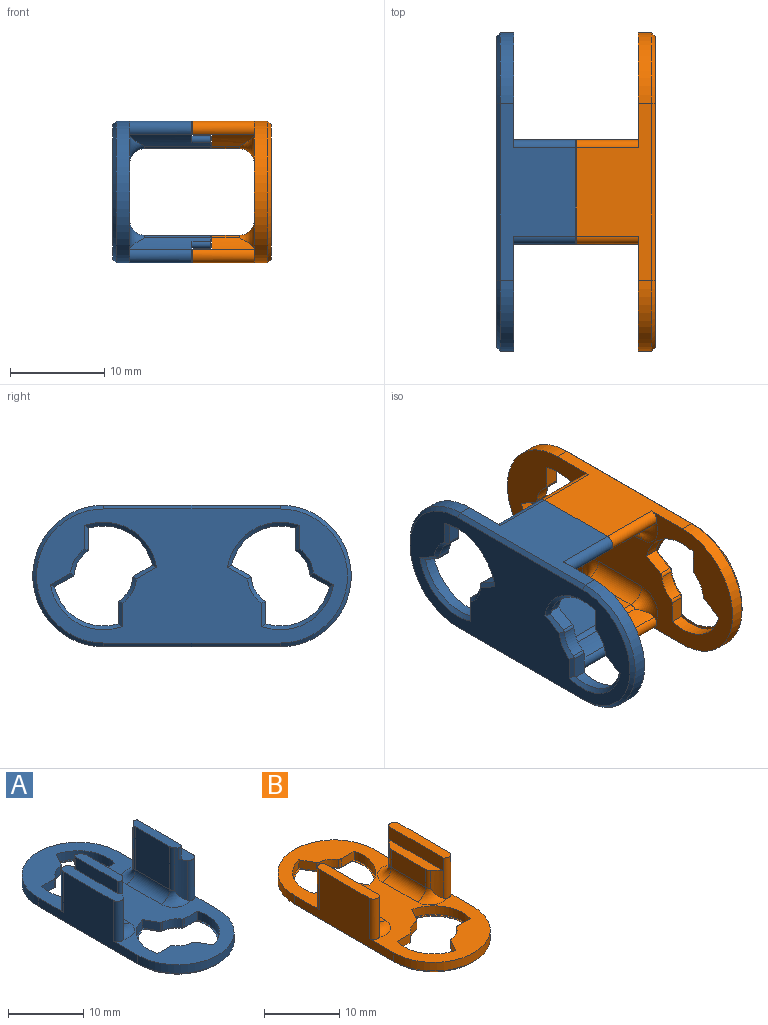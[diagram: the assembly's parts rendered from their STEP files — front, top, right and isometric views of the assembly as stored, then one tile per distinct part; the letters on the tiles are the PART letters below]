
ASSEMBLY  parts=2 mates=1
PART A: 84 faces, bbox 15x33.8x10.4 mm
  f0: plane 11x2.24mm, normal (0,0,1), area 17mm2, adj f3,f15,f16,f20,f21,f60,f64,f65
  f1: plane 32.95x14.2mm, normal (0,0,-1), area 269mm2, adj f22,f23,f24,f25,f48,f49,f50,f51
  f2: plane 33.75x15mm, normal (0,0,1), area 226mm2, adj f3,f5,f7,f8,f9,f14,f15,f21
  f3: plane 18.75x8mm, normal (1,0,0), area 88.3mm2, adj f0,f2,f7,f8,f15,f21,f23
  f4: plane 7x6.49mm, normal (1,0,0), area 45.4mm2, adj f11,f12,f30,f63
  f5: plane 18.75x8mm, normal (-1,0,0), area 88.3mm2, adj f2,f6,f7,f8,f9,f14,f24
  f6: plane 11x2.24mm, normal (0,0,1), area 17mm2, adj f5,f9,f10,f13,f14,f62,f66,f67
  f7: cylinder r=7.5mm len=15mm, axis (0,0,-1), area 33mm2, adj f2,f3,f5,f22
  f8: cylinder r=7.5mm len=15mm, axis (0,0,-1), area 33mm2, adj f2,f3,f5,f25
  f9: cylinder r=0.8mm len=6.6mm, axis (0,0,1), area 13.4mm2, adj f2,f5,f6,f10,f29
  f10: cylinder r=7.37mm len=8.55mm, axis (0,0,1), area 11.6mm2, adj f6,f9,f11,f29,f63,f66
  f11: cylinder r=0.8mm len=7mm, axis (0,0,1), area 4.8mm2, adj f4,f10,f29,f63
  f12: cylinder r=0.8mm len=7mm, axis (0,0,1), area 4.8mm2, adj f4,f13,f31,f63
  f13: cylinder r=7.37mm len=8.55mm, axis (0,0,1), area 11.6mm2, adj f6,f12,f14,f31,f63,f67
  f14: cylinder r=0.8mm len=6.6mm, axis (0,0,1), area 13.4mm2, adj f2,f5,f6,f13,f31
  f15: cylinder r=0.8mm len=6.6mm, axis (0,0,1), area 13.4mm2, adj f0,f2,f3,f16,f26
  f16: cylinder r=7.37mm len=8.55mm, axis (0,0,1), area 11.6mm2, adj f0,f15,f17,f26,f61,f64
  f17: cylinder r=0.8mm len=7mm, axis (0,0,1), area 4.8mm2, adj f16,f18,f26,f61
  f18: plane 7x6.49mm, normal (-1,0,0), area 45.4mm2, adj f17,f19,f27,f61
  f19: cylinder r=0.8mm len=7mm, axis (0,0,1), area 4.8mm2, adj f18,f20,f28,f61
  f20: cylinder r=7.37mm len=8.55mm, axis (0,0,1), area 11.6mm2, adj f0,f19,f21,f28,f61,f65
  f21: cylinder r=0.8mm len=6.6mm, axis (0,0,1), area 13.4mm2, adj f0,f2,f3,f20,f28
  f22: cone r=7.5mm half-angle=45deg, axis (0,0,1), area 13mm2, adj f1,f7,f23,f24
  f23: plane 18.75x0.4mm, normal (0.71,0,-0.71), area 10.6mm2, adj f1,f3,f22,f25
  f24: plane 18.75x0.4mm, normal (-0.71,0,-0.71), area 10.6mm2, adj f1,f5,f22,f25
  f25: cone r=7.5mm half-angle=45deg, axis (0,0,1), area 13mm2, adj f1,f8,f23,f24
  f26: torus R=2.4mm, axis (0,0,1), area 5.8mm2, adj f2,f15,f16,f17,f27
  f27: cylinder r=1.6mm len=6.49mm, axis (0,1,0), area 16.3mm2, adj f2,f18,f26,f28
  f28: torus R=2.4mm, axis (0,0,1), area 5.8mm2, adj f2,f19,f20,f21,f27
  f29: torus R=2.4mm, axis (0,0,1), area 5.8mm2, adj f2,f9,f10,f11,f30
  f30: cylinder r=1.6mm len=6.49mm, axis (0,-1,0), area 16.3mm2, adj f2,f4,f29,f31
  f31: torus R=2.4mm, axis (0,0,1), area 5.8mm2, adj f2,f12,f13,f14,f30
  f32: cylinder r=5.55mm len=6.98mm, axis (0,0,1), area 12.6mm2, adj f2,f33,f39,f68
  f33: plane 2.43x1.4mm, normal (0,-1,0), area 3.4mm2, adj f2,f32,f55,f68,f78
  f34: cylinder r=3.1mm len=2.3mm, axis (0,0,1), area 3.8mm2, adj f2,f57,f78,f79
  f35: plane 2.12x1.4mm, normal (-0.87,-0.5,0), area 3.4mm2, adj f2,f36,f59,f69,f79
  f36: cylinder r=5.55mm len=6.98mm, axis (0,0,1), area 12.6mm2, adj f2,f35,f37,f69
  f37: plane 2.43x1.4mm, normal (0,1,0), area 3.4mm2, adj f2,f36,f58,f69,f76
  f38: cylinder r=3.1mm len=2.3mm, axis (0,0,1), area 3.8mm2, adj f2,f56,f76,f77
  f39: plane 2.12x1.4mm, normal (0.87,0.5,0), area 3.4mm2, adj f2,f32,f54,f68,f77
  f40: plane 2.12x1.4mm, normal (-0.87,0.5,0), area 3.4mm2, adj f2,f47,f51,f71,f80
  f41: cylinder r=3.1mm len=2.3mm, axis (0,0,1), area 3.8mm2, adj f2,f52,f80,f83
  f42: plane 2.43x1.4mm, normal (0,1,0), area 3.4mm2, adj f2,f43,f53,f70,f83
  f43: cylinder r=5.55mm len=6.98mm, axis (0,0,1), area 12.6mm2, adj f2,f42,f44,f70
  f44: plane 2.12x1.4mm, normal (0.87,-0.5,0), area 3.4mm2, adj f2,f43,f50,f70,f82
  f45: cylinder r=3.1mm len=2.3mm, axis (0,0,1), area 3.8mm2, adj f2,f49,f81,f82
  f46: plane 2.43x1.4mm, normal (0,-1,0), area 3.4mm2, adj f2,f47,f48,f71,f81
  f47: cylinder r=5.55mm len=6.98mm, axis (0,0,1), area 12.6mm2, adj f2,f40,f46,f71
  f48: plane 2.67x0.42mm, normal (0,-0.71,-0.71), area 1.4mm2, adj f1,f46,f49,f74,f81
  f49: cone r=3.5mm half-angle=45deg, axis (0,0,-1), area 1.8mm2, adj f1,f45,f48,f50,f81,f82
  f50: plane 2.5x1.46mm, normal (0.61,-0.35,-0.71), area 1.4mm2, adj f1,f44,f49,f75,f82
  f51: plane 2.5x1.46mm, normal (-0.61,0.35,-0.71), area 1.4mm2, adj f1,f40,f52,f74,f80
  f52: cone r=3.5mm half-angle=45deg, axis (0,0,-1), area 1.8mm2, adj f1,f41,f51,f53,f80,f83
  f53: plane 2.67x0.42mm, normal (0,0.71,-0.71), area 1.4mm2, adj f1,f42,f52,f75,f83
  f54: plane 2.5x1.46mm, normal (0.61,0.35,-0.71), area 1.4mm2, adj f1,f39,f56,f72,f77
  f55: plane 2.67x0.42mm, normal (0,-0.71,-0.71), area 1.4mm2, adj f1,f33,f57,f72,f78
  f56: cone r=3.1mm half-angle=45deg, axis (0,0,-1), area 1.8mm2, adj f1,f38,f54,f58,f76,f77
  f57: cone r=3.1mm half-angle=45deg, axis (0,0,-1), area 1.8mm2, adj f1,f34,f55,f59,f78,f79
  f58: plane 2.67x0.42mm, normal (0,0.71,-0.71), area 1.4mm2, adj f1,f37,f56,f73,f76
  f59: plane 2.5x1.46mm, normal (-0.61,-0.35,-0.71), area 1.4mm2, adj f1,f35,f57,f73,f79
  f60: plane 7.88x2mm, normal (1,0,0), area 15.7mm2, adj f0,f61,f64,f65
  f61: plane 8.68x1.35mm, normal (0,0,1), area 11mm2, adj f16,f17,f18,f19,f20,f60,f64,f65
  f62: plane 7.88x2mm, normal (-1,0,0), area 15.7mm2, adj f6,f63,f66,f67
  f63: plane 8.68x1.35mm, normal (0,0,1), area 11mm2, adj f4,f10,f11,f12,f13,f62,f66,f67
  f64: cylinder r=0.4mm len=2mm, axis (0,0,1), area 1.9mm2, adj f0,f16,f60,f61
  f65: cylinder r=0.4mm len=2mm, axis (0,0,1), area 1.9mm2, adj f0,f20,f60,f61
  f66: cylinder r=0.4mm len=2mm, axis (0,0,1), area 1.9mm2, adj f6,f10,f62,f63
  f67: cylinder r=0.4mm len=2mm, axis (0,0,1), area 1.9mm2, adj f6,f13,f62,f63
  f68: plane 6.98x4.41mm, normal (0,0,1), area 2.2mm2, adj f32,f33,f39,f72
  f69: plane 6.98x4.41mm, normal (0,0,1), area 2.2mm2, adj f35,f36,f37,f73
  f70: plane 6.98x4.41mm, normal (0,0,1), area 2.2mm2, adj f42,f43,f44,f75
  f71: plane 6.98x4.41mm, normal (0,0,1), area 2.2mm2, adj f40,f46,f47,f74
  f72: cone r=5.7mm half-angle=45deg, axis (0,0,-1), area 5.3mm2, adj f1,f54,f55,f68
  f73: cone r=5.7mm half-angle=45deg, axis (0,0,-1), area 5.3mm2, adj f1,f58,f59,f69
  f74: cone r=5.7mm half-angle=45deg, axis (0,0,-1), area 5.3mm2, adj f1,f48,f51,f71
  f75: cone r=5.7mm half-angle=45deg, axis (0,0,-1), area 5.3mm2, adj f1,f50,f53,f70
  f76: cylinder r=0.4mm len=1.45mm, axis (0,0,1), area 0.6mm2, adj f2,f37,f38,f56,f58
  f77: cylinder r=0.4mm len=1.45mm, axis (0,0,1), area 0.5mm2, adj f2,f38,f39,f54,f56
  f78: cylinder r=0.4mm len=1.45mm, axis (0,0,1), area 0.6mm2, adj f2,f33,f34,f55,f57
  f79: cylinder r=0.4mm len=1.45mm, axis (0,0,1), area 0.5mm2, adj f2,f34,f35,f57,f59
  f80: cylinder r=0.4mm len=1.45mm, axis (0,0,1), area 0.5mm2, adj f2,f40,f41,f51,f52
  f81: cylinder r=0.4mm len=1.45mm, axis (0,0,1), area 0.6mm2, adj f2,f45,f46,f48,f49
  f82: cylinder r=0.4mm len=1.45mm, axis (0,0,1), area 0.5mm2, adj f2,f44,f45,f49,f50
  f83: cylinder r=0.4mm len=1.45mm, axis (0,0,1), area 0.6mm2, adj f2,f41,f42,f52,f53
PART B: 80 faces, bbox 15x33.8x8.4 mm
  f0: plane 2.5x1.46mm, normal (-0.61,0.35,-0.71), area 1.4mm2, adj f13,f53,f58,f70,f72
  f1: plane 2.67x0.42mm, normal (0,-0.71,-0.71), area 1.4mm2, adj f13,f51,f59,f70,f74
  f2: plane 2.67x0.42mm, normal (0,0.71,-0.71), area 1.4mm2, adj f13,f55,f58,f71,f73
  f3: plane 2.5x1.46mm, normal (0.61,-0.35,-0.71), area 1.4mm2, adj f13,f49,f59,f71,f75
  f4: plane 2.5x1.46mm, normal (0.61,0.35,-0.71), area 1.4mm2, adj f13,f41,f56,f69,f77
  f5: plane 2.67x0.42mm, normal (0,-0.71,-0.71), area 1.4mm2, adj f13,f43,f57,f69,f78
  f6: plane 2.67x0.42mm, normal (0,0.71,-0.71), area 1.4mm2, adj f13,f47,f56,f68,f76
  f7: plane 2.5x1.46mm, normal (-0.61,-0.35,-0.71), area 1.4mm2, adj f13,f45,f57,f68,f79
  f8: plane 6.49x2.9mm, normal (1,0,0), area 18.8mm2, adj f9,f23,f38,f63
  f9: cylinder r=0.8mm len=2.9mm, axis (0,0,1), area 2mm2, adj f8,f10,f39,f63
  f10: cylinder r=7.37mm len=4.45mm, axis (0,0,1), area 6.8mm2, adj f9,f24,f39,f63
  f11: cylinder r=0.8mm len=2.9mm, axis (0,0,1), area 2mm2, adj f12,f28,f36,f61
  f12: cylinder r=7.37mm len=4.45mm, axis (0,0,1), area 6.8mm2, adj f11,f29,f36,f61
  f13: plane 32.95x14.2mm, normal (0,0,-1), area 269mm2, adj f0,f1,f2,f3,f4,f5,f6,f7
  f14: plane 33.75x15mm, normal (0,0,1), area 226mm2, adj f15,f16,f18,f19,f21,f24,f25,f29
  f15: plane 18.75x8mm, normal (1,0,0), area 88.3mm2, adj f14,f18,f19,f20,f25,f29,f31
  f16: plane 18.75x8mm, normal (-1,0,0), area 88.3mm2, adj f14,f17,f18,f19,f21,f24,f32
  f17: plane 11x1.45mm, normal (0,0,1), area 15.5mm2, adj f16,f21,f24,f62
  f18: cylinder r=7.5mm len=15mm, axis (0,0,-1), area 33mm2, adj f14,f15,f16,f30
  f19: cylinder r=7.5mm len=15mm, axis (0,0,-1), area 33mm2, adj f14,f15,f16,f33
  f20: plane 11x1.45mm, normal (0,0,1), area 15.5mm2, adj f15,f25,f29,f60
  f21: cylinder r=0.8mm len=6.6mm, axis (0,0,1), area 13.3mm2, adj f14,f16,f17,f22,f37,f62,f63
  f22: cylinder r=7.37mm len=4.45mm, axis (0,0,1), area 6.8mm2, adj f21,f23,f37,f63
  f23: cylinder r=0.8mm len=2.9mm, axis (0,0,1), area 2mm2, adj f8,f22,f37,f63
  f24: cylinder r=0.8mm len=6.6mm, axis (0,0,1), area 13.3mm2, adj f10,f14,f16,f17,f39,f62,f63
  f25: cylinder r=0.8mm len=6.6mm, axis (0,0,1), area 13.3mm2, adj f14,f15,f20,f26,f34,f60,f61
  f26: cylinder r=7.37mm len=4.45mm, axis (0,0,1), area 6.8mm2, adj f25,f27,f34,f61
  f27: cylinder r=0.8mm len=2.9mm, axis (0,0,1), area 2mm2, adj f26,f28,f34,f61
  f28: plane 6.49x2.9mm, normal (-1,0,0), area 18.8mm2, adj f11,f27,f35,f61
  f29: cylinder r=0.8mm len=6.6mm, axis (0,0,1), area 13.3mm2, adj f12,f14,f15,f20,f36,f60,f61
  f30: cone r=7.5mm half-angle=45deg, axis (0,0,1), area 13mm2, adj f13,f18,f31,f32
  f31: plane 18.75x0.4mm, normal (0.71,0,-0.71), area 10.6mm2, adj f13,f15,f30,f33
  f32: plane 18.75x0.4mm, normal (-0.71,0,-0.71), area 10.6mm2, adj f13,f16,f30,f33
  f33: cone r=7.5mm half-angle=45deg, axis (0,0,1), area 13mm2, adj f13,f19,f31,f32
  f34: torus R=2.4mm, axis (0,0,1), area 5.8mm2, adj f14,f25,f26,f27,f35
  f35: cylinder r=1.6mm len=6.49mm, axis (0,1,0), area 16.3mm2, adj f14,f28,f34,f36
  f36: torus R=2.4mm, axis (0,0,1), area 5.8mm2, adj f11,f12,f14,f29,f35
  f37: torus R=2.4mm, axis (0,0,1), area 5.8mm2, adj f14,f21,f22,f23,f38
  f38: cylinder r=1.6mm len=6.49mm, axis (0,-1,0), area 16.3mm2, adj f8,f14,f37,f39
  f39: torus R=2.4mm, axis (0,0,1), area 5.8mm2, adj f9,f10,f14,f24,f38
  f40: cylinder r=3.1mm len=2.3mm, axis (0,0,1), area 3.8mm2, adj f14,f56,f76,f77
  f41: plane 2.12x1.4mm, normal (0.87,0.5,0), area 3.4mm2, adj f4,f14,f42,f65,f77
  f42: cylinder r=5.55mm len=6.98mm, axis (0,0,1), area 12.6mm2, adj f14,f41,f43,f65
  f43: plane 2.43x1.4mm, normal (0,-1,0), area 3.4mm2, adj f5,f14,f42,f65,f78
  f44: cylinder r=3.1mm len=2.3mm, axis (0,0,1), area 3.8mm2, adj f14,f57,f78,f79
  f45: plane 2.12x1.4mm, normal (-0.87,-0.5,0), area 3.4mm2, adj f7,f14,f46,f64,f79
  f46: cylinder r=5.55mm len=6.98mm, axis (0,0,1), area 12.6mm2, adj f14,f45,f47,f64
  f47: plane 2.43x1.4mm, normal (0,1,0), area 3.4mm2, adj f6,f14,f46,f64,f76
  f48: cylinder r=5.55mm len=6.98mm, axis (0,0,1), area 12.6mm2, adj f14,f49,f55,f66
  f49: plane 2.12x1.4mm, normal (0.87,-0.5,0), area 3.4mm2, adj f3,f14,f48,f66,f75
  f50: cylinder r=3.1mm len=2.3mm, axis (0,0,1), area 3.8mm2, adj f14,f59,f74,f75
  f51: plane 2.43x1.4mm, normal (0,-1,0), area 3.4mm2, adj f1,f14,f52,f67,f74
  f52: cylinder r=5.55mm len=6.98mm, axis (0,0,1), area 12.6mm2, adj f14,f51,f53,f67
  f53: plane 2.12x1.4mm, normal (-0.87,0.5,0), area 3.4mm2, adj f0,f14,f52,f67,f72
  f54: cylinder r=3.1mm len=2.3mm, axis (0,0,1), area 3.8mm2, adj f14,f58,f72,f73
  f55: plane 2.43x1.4mm, normal (0,1,0), area 3.4mm2, adj f2,f14,f48,f66,f73
  f56: cone r=3.1mm half-angle=45deg, axis (0,0,-1), area 1.8mm2, adj f4,f6,f13,f40,f76,f77
  f57: cone r=3.1mm half-angle=45deg, axis (0,0,-1), area 1.8mm2, adj f5,f7,f13,f44,f78,f79
  f58: cone r=3.5mm half-angle=45deg, axis (0,0,-1), area 1.8mm2, adj f0,f2,f13,f54,f72,f73
  f59: cone r=3.5mm half-angle=45deg, axis (0,0,-1), area 1.8mm2, adj f1,f3,f13,f50,f74,f75
  f60: plane 10.33x2.1mm, normal (-1,0,0), area 21.7mm2, adj f20,f25,f29,f61
  f61: plane 10.33x1.45mm, normal (0,0,1), area 12.5mm2, adj f11,f12,f25,f26,f27,f28,f29,f60
  f62: plane 10.33x2.1mm, normal (1,0,0), area 21.7mm2, adj f17,f21,f24,f63
  f63: plane 10.33x1.45mm, normal (0,0,1), area 12.5mm2, adj f8,f9,f10,f21,f22,f23,f24,f62
  f64: plane 6.98x4.41mm, normal (0,0,1), area 2.2mm2, adj f45,f46,f47,f68
  f65: plane 6.98x4.41mm, normal (0,0,1), area 2.2mm2, adj f41,f42,f43,f69
  f66: plane 6.98x4.41mm, normal (0,0,1), area 2.2mm2, adj f48,f49,f55,f71
  f67: plane 6.98x4.41mm, normal (0,0,1), area 2.2mm2, adj f51,f52,f53,f70
  f68: cone r=5.3mm half-angle=45deg, axis (0,0,-1), area 5.3mm2, adj f6,f7,f13,f64
  f69: cone r=5.3mm half-angle=45deg, axis (0,0,-1), area 5.3mm2, adj f4,f5,f13,f65
  f70: cone r=5.3mm half-angle=45deg, axis (0,0,-1), area 5.3mm2, adj f0,f1,f13,f67
  f71: cone r=5.3mm half-angle=45deg, axis (0,0,-1), area 5.3mm2, adj f2,f3,f13,f66
  f72: cylinder r=0.4mm len=1.45mm, axis (0,0,1), area 0.5mm2, adj f0,f14,f53,f54,f58
  f73: cylinder r=0.4mm len=1.45mm, axis (0,0,1), area 0.6mm2, adj f2,f14,f54,f55,f58
  f74: cylinder r=0.4mm len=1.45mm, axis (0,0,1), area 0.6mm2, adj f1,f14,f50,f51,f59
  f75: cylinder r=0.4mm len=1.45mm, axis (0,0,1), area 0.5mm2, adj f3,f14,f49,f50,f59
  f76: cylinder r=0.4mm len=1.45mm, axis (0,0,1), area 0.6mm2, adj f6,f14,f40,f47,f56
  f77: cylinder r=0.4mm len=1.45mm, axis (0,0,1), area 0.5mm2, adj f4,f14,f40,f41,f56
  f78: cylinder r=0.4mm len=1.45mm, axis (0,0,1), area 0.6mm2, adj f5,f14,f43,f44,f57
  f79: cylinder r=0.4mm len=1.45mm, axis (0,0,1), area 0.5mm2, adj f7,f14,f44,f45,f57
PLACE A rot(axis=(0,1,0),90deg) t=(21.35,3.08,5.87)mm
PLACE B rot(axis=(0,-1,0),90deg) t=(38.15,3.08,-11.13)mm
MATE fastened A.f6 <-> B.f20  axis (1,0,0) through (29.75,-1.62,13.37)mm
